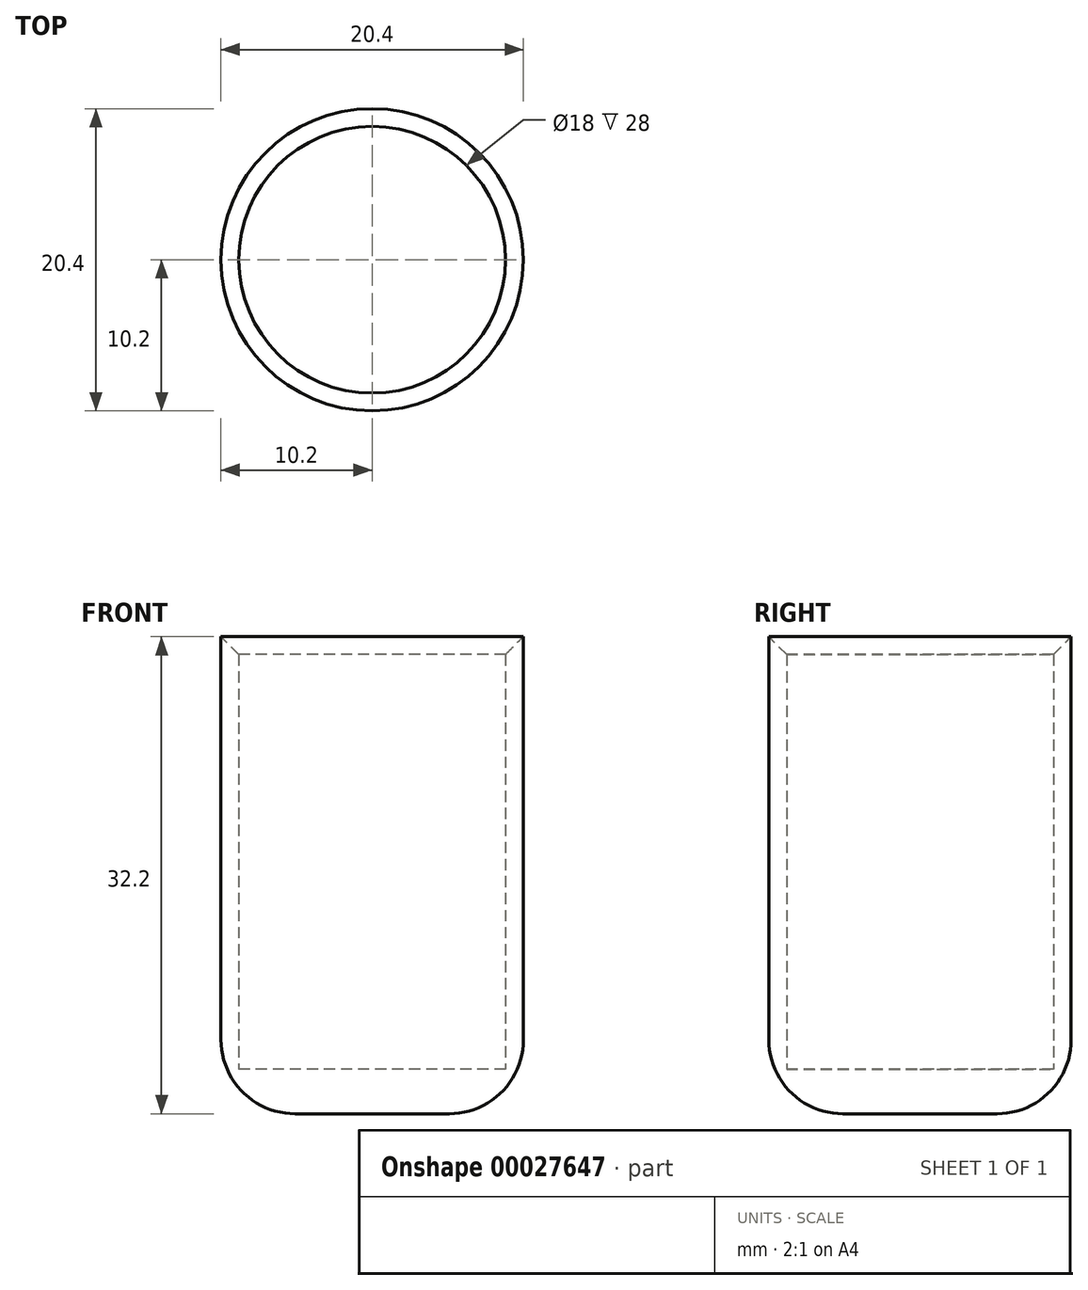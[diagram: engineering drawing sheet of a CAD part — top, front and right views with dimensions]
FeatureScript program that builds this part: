
annotation { "Feature Type Name" : "Feature", "Feature Type Description" : "" }
export const myFeature = defineFeature(function(context is Context, id is Id, definition is map)
    precondition{}
    {
        {
            var Q0;
            Q0=qCreatedBy(makeId("Top.planeOp"),FACE);
            var sketch = newSketch(context, id + "F0", { "sketchPlane" : qUnion([Q0])});
            skCircle(sketch, "E0", {"center": v(0, 0) * mm, "radius": 9 * mm});
            skCircle(sketch, "E1", {"center": v(0, 0) * mm, "radius": 10.2 * mm});
            skSolve(sketch);
        }
        {
            var Q0;
            Q0=makeQuery(id+"F0.imprint","IMPRINT",FACE,{"disambiguationData":[TD([[makeQuery(id+"F0.imprint","IMPRINT",EDGE,{"derivedFrom":sQuery(id+"F0.wireOp",EDGE,"E0")}),1.0]])]});
            extrude(context, id + "F1", {"entities" : qUnion([Q0]), "depth" : 3 * mm});
        }
        {
            var Q0;
            Q0 = qSketchRegion(id + "F0", true);
            extrude(context, id + "F2", {"entities" : qUnion([Q0]), "operationType" : NewBodyOperationType.ADD, "depth" : 36 * mm});
        }
        {
            var Q0;
            Q0=makeQuery(id+"F2.opExtrude","CAP_EDGE",EDGE,{"disambiguationData":[OSD([sQuery(id+"F0.wireOp",EDGE,"E0")])],"isStart":false});
            chamfer(context, id + "F3", {"entities" : qUnion([Q0]), "width" : 5 * mm, "tangentPropagation" : true});
        }
        {
            var Q0;
            Q0=makeQuery(id+"F2.opExtrude","CAP_EDGE",EDGE,{"disambiguationData":[OSD([sQuery(id+"F0.wireOp",EDGE,"E1")])],"isStart":true});
            fillet(context, id + "F4", {"entities" : qUnion([Q0]), "radius" : 5 * mm, "tangentPropagation" : true, "allowEdgeOverflow" : false});
        }
    });
